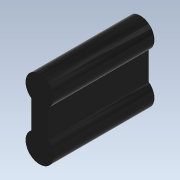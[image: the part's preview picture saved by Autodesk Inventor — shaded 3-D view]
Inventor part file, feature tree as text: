
AUTODESK INVENTOR PART (.ipt)
format: ipt  version: 2020.2 (Build 242310000, 310)  size: 91,648 bytes
history: native  units: mm
features: extrude x1, sketch x1
ambient origin geometry x8: Origin, YZ Plane, XZ Plane, XY Plane, X Axis, Y Axis, Z Axis, Center Point
bodies: Solid1 (feature_tree)
feature tree (2):
  extrude  "Extrusion1"  Depth=18.0mm
  sketch  "Sketch1"  dims[d0=5.0mm d1=18.0mm d2=5.0mm d3=1.5mm d4=1.5mm d5=18.0mm d6=0.0mm]
